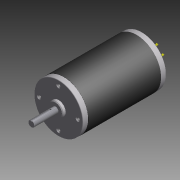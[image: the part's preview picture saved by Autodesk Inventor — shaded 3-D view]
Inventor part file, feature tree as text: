
AUTODESK INVENTOR PART (.ipt)
format: ipt  version: 2011 (Build 150239000, 239)  size: 219,648 bytes
history: native  units: mm (DEFAULTED — no unit token found)
features: sketch x10, extrude x7, other x7, chamfer x4, pattern_circular x3, plane x3, hole x2, fillet x2, revolve x1
ambient origin geometry x8: Origin, YZ Plane, XZ Plane, XY Plane, X Axis, Y Axis, Z Axis, Center Point
bodies: Solid1 (feature_tree)
feature tree (39):
  extrude  "Extrusion1"  Depth=7.0mm TaperAngle=0.0deg
  extrude  "Extrusion2"  Depth=3.9878mm TaperAngle=0.0deg
  chamfer  "Chamfer1"  Distance=1.0mm
  hole  "Hole2"  [1 undecoded]
  pattern_circular  "Circular Pattern2"  Count=4 Angle=90.0deg
  chamfer  "Chamfer3"  Distance=31.623mm
  extrude  "Extrusion3"  Depth=12.7mm
  fillet  "Fillet1"  Radius=2.0mm
  extrude  "Extrusion4"  Depth=25.6286mm TaperAngle=0.0deg
  extrude  "Extrusion5"  Depth=95.6056mm TaperAngle=0.0deg
  extrude  "Extrusion6"  Depth=7.0mm TaperAngle=0.0deg
  extrude  "Extrusion7"  Depth=4.1148mm TaperAngle=0.0deg
  hole  "Hole3"  [1 undecoded]
  chamfer  "Chamfer2"  Distance=0.762mm
  pattern_circular  "Circular Pattern3"  [2 undecoded]
  fillet  "Fillet2"  Radius=20.0mm
  chamfer  "Chamfer4"  Distance=0.25mm
  plane  "Work Plane1"
  revolve  "Revolution1"  Angle=45.0deg
  other  "Work Axis1"
  other  "Work Point1"
  other  "Work Point2"
  other  "Work Point3"
  pattern_circular  "Circular Pattern4"  Angle=330.0deg  [1 undecoded]
  sketch  "Sketch1"  dims[d0=64.008mm d1=7.0mm d2=0.0mm]
  sketch  "Sketch2"  dims[d3=19.05mm d4=3.9878mm d5=0.0mm d6=1.0mm d7=1.0mm]
  sketch  "Sketch4"  dims[d18=3.9624mm d19=9.525mm d20=6.35mm d21=60.0deg d22=19.05mm d23=20.594885mm d24=25.4mm d25=40.0mm d27=90.0deg]
  sketch  "Sketch5"  dims[d28=7.9502mm d29=31.623mm d30=0.0mm]
  sketch  "Sketch7"  dims[d31=0.79375mm d33=12.7mm d34=2.0mm]
  sketch  "Sketch8"  dims[d35=3.0mm d36=25.6286mm d37=0.0mm]
  sketch  "Sketch9"  dims[d38=64.4144mm d39=95.6056mm d40=0.0mm]
  sketch  "Sketch10"  dims[d41=64.008mm d42=7.0mm d43=0.0mm]
  sketch  "Sketch11"  dims[d44=30.1498mm d45=4.1148mm d46=0.0mm]
  sketch  "Sketch12"  dims[d47=5.08mm d48=12.7mm d49=9.906mm d50=4.572mm d51=14.3117mm d52=7.62mm d53=20.594885mm d54=0.508mm d55=3.175mm d56=0.762mm d57=0.762mm d58=3.175mm d59=20.0mm d61=360.0deg d62=0.25mm d63=3.175mm d64=45.0deg d65=45.0deg d66=45.0deg d67=45.0deg d68=330.0deg d69=3.683mm d70=2.54mm d71=7.366mm d72=90.0deg d73=3.175mm d74=6.35mm d75=20.0mm d76=30.0deg d78=60.0deg]
  plane  "Work Plane2"
  plane  "Work Plane3"
  other  "Work Point4"
  other  "Work Point5"
  other  "Work Point6"
note: 5 required parameter values undecoded (feature->parameter linkage not recoverable at this tier; creation-order binding heuristic only, values carry confidence <= 0.55)
